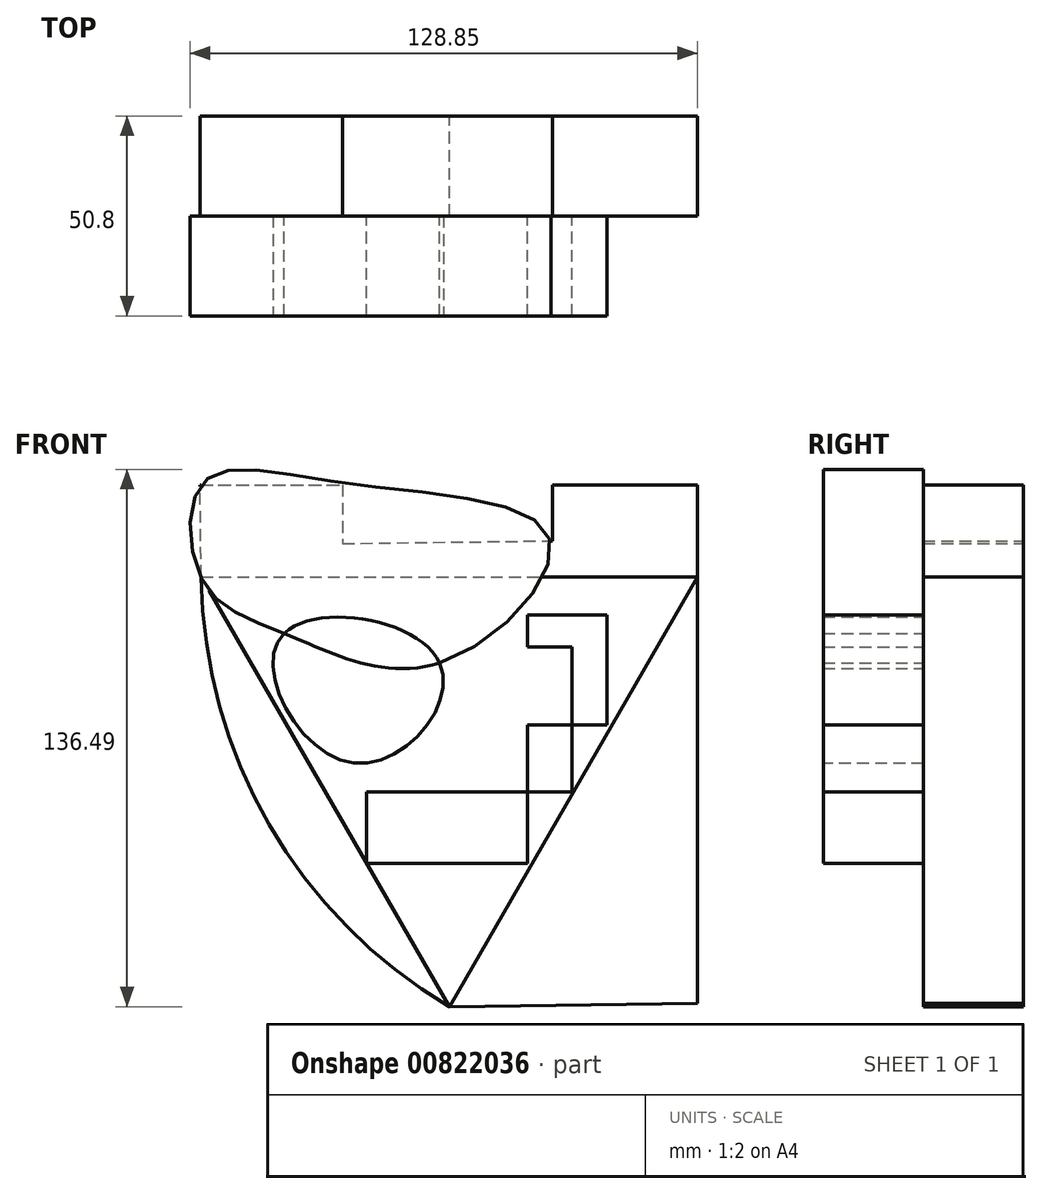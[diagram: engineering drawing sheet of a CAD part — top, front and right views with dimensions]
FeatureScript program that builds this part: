
annotation { "Feature Type Name" : "Feature", "Feature Type Description" : "" }
export const myFeature = defineFeature(function(context is Context, id is Id, definition is map)
    precondition{}
    {
        {
            var Q0;
            Q0=qCreatedBy(makeId("Front.planeOp"),FACE);
            var sketch = newSketch(context, id + "F0", { "sketchPlane" : qUnion([Q0])});
            skCircle(sketch, "E0.cCircle", {"center": v(-2.98, 2.26) * mm, "radius": 36.39 * mm, "construction": true});
            skLineSegment(sketch, "E0.0", {"start": v(-66, 38.65) * mm, "end": v(60.05, 38.65) * mm});
            skLineSegment(sketch, "E0.1", {"start": v(60.05, 38.65) * mm, "end": v(-2.98, -70.52) * mm});
            skLineSegment(sketch, "E0.2", {"start": v(-2.98, -70.52) * mm, "end": v(-66, 38.65) * mm});
            skPoint(sketch, "E0.0.midPoint", {"position": v(-2.98, 38.65) * mm});
            skLineSegment(sketch, "E1", {"start": v(60.05, 38.65) * mm, "end": v(60.05, -69.7) * mm});
            skLineSegment(sketch, "E2", {"start": v(60.05, -69.7) * mm, "end": v(-2.98, -70.52) * mm});
            skLineSegment(sketch, "E3", {"start": v(-66, 38.65) * mm, "end": v(-66.3, 62.08) * mm});
            skLineSegment(sketch, "E4", {"start": v(-66.3, 62.08) * mm, "end": v(-30.07, 62.08) * mm});
            skLineSegment(sketch, "E5", {"start": v(-30.07, 62.08) * mm, "end": v(-30.07, 47.14) * mm});
            skLineSegment(sketch, "E6", {"start": v(-30.07, 47.14) * mm, "end": v(-2.98, 47.49) * mm});
            skLineSegment(sketch, "E7", {"start": v(-2.98, 47.49) * mm, "end": v(-2.98, 62.08) * mm});
            skLineSegment(sketch, "E8", {"start": v(-2.98, 62.08) * mm, "end": v(-2.98, 47.49) * mm});
            skLineSegment(sketch, "E9", {"start": v(-2.98, 47.49) * mm, "end": v(23.3, 47.83) * mm});
            skLineSegment(sketch, "E10", {"start": v(23.3, 47.83) * mm, "end": v(23.3, 62.08) * mm});
            skLineSegment(sketch, "E11", {"start": v(23.3, 62.08) * mm, "end": v(60.05, 62.08) * mm});
            skLineSegment(sketch, "E12", {"start": v(60.05, 62.08) * mm, "end": v(60.05, 38.65) * mm});
            skArc(sketch, "E13", {"start": v(-2.98, 62.08) * mm, "mid": v(-16.52, 68.36) * mm, "end": v(-30.07, 62.08) * mm});
            skArc(sketch, "E14", {"start": v(23.3, 62.08) * mm, "mid": v(10.16, 68.26) * mm, "end": v(-2.98, 62.08) * mm});
            skArc(sketch, "E15", {"start": v(-66, 38.65) * mm, "mid": v(-48.74, -24.16) * mm, "end": v(-2.98, -70.52) * mm});
            skSolve(sketch);
        }
        {
            var Q0;
            Q0=makeQuery(id+"F0.imprint","IMPRINT",FACE,{"disambiguationData":[TD([[makeQuery(id+"F0.imprint","IMPRINT",EDGE,{"derivedFrom":sQuery(id+"F0.wireOp",EDGE,"E0.0")}),1.0]])]});
            var Q1;
            Q1=makeQuery(id+"F0.imprint","IMPRINT",FACE,{"disambiguationData":[TD([[makeQuery(id+"F0.imprint","IMPRINT",EDGE,{"derivedFrom":sQuery(id+"F0.wireOp",EDGE,"E0.2")}),1.0]])]});
            var Q2;
            Q2=makeQuery(id+"F0.imprint","IMPRINT",FACE,{"disambiguationData":[TD([[makeQuery(id+"F0.imprint","IMPRINT",EDGE,{"derivedFrom":sQuery(id+"F0.wireOp",EDGE,"E0.1")}),1.0]])]});
            extrude(context, id + "F1", {"entities" : qUnion([Q0, Q1, Q2]), "depth" : 25.4 * mm, "offsetDistance" : 25.4 * mm});
        }
        {
            var Q0;
            Q0=makeQuery(id+"F1.opExtrude","CAP_FACE",FACE,{"disambiguationData":[OSD([sQuery(id+"F0.wireOp",EDGE,"E0.1"),sQuery(id+"F0.wireOp",EDGE,"E1"),sQuery(id+"F0.wireOp",EDGE,"E2")])],"isStart":false});
            var sketch = newSketch(context, id + "F2", { "sketchPlane" : qUnion([Q0])});
            skSolve(sketch);
        }
        {
            var Q0;
            Q0=makeQuery(id+"F2.imprint","IMPRINT",FACE,{"disambiguationData":[TD([[makeQuery(id+"F2.imprint","IMPRINT",EDGE,{"derivedFrom":makeQuery(id+"F1.opExtrude","CAP_EDGE",EDGE,{"disambiguationData":[OSD([sQuery(id+"F0.wireOp",EDGE,"E0.1")])],"isStart":false})}),1.0]])]});
            var sketch = newSketch(context, id + "F3", { "sketchPlane" : qUnion([Q0])});
            skFitSpline(sketch, "E16", {"points": [v(-45.83, 23.3) * mm, v(-5.4, 16.82) * mm, v(-27.24, -8.65) * mm, v(-45.83, 23.3) * mm]});
            skFitSpline(sketch, "E17", {"points": [v(-65.65, 62.52) * mm, v(-29.66, 62.52) * mm, v(22.5, 48.36) * mm, v(-5.4, 16.82) * mm, v(-44.9, 24.35) * mm, v(-65.24, 37.04) * mm, v(-65.65, 62.52) * mm]});
            skSolve(sketch);
        }
        {
            var Q0;
            {var subQ0=sQuery(id+"F3.wireOp",EDGE,"E17");var subQ1=sQuery(id+"F3.wireOp",EDGE,"E16");var subQ2=makeQuery(id+"F3.imprint","INTERSECT",VERTEX,{"disambiguationData":[OD(0.0)],"derivedFrom":[subQ1,subQ0]});Q0=makeQuery(id+"F3.imprint","IMPRINT",FACE,{"disambiguationData":[TD([[makeQuery(id+"F3.imprint","IMPRINT",EDGE,{"disambiguationData":[TD([[subQ2,1.0]])],"derivedFrom":subQ1}),-1.0]])]});}
            var Q1;
            {var subQ0=sQuery(id+"F3.wireOp",EDGE,"E17");var subQ1=sQuery(id+"F3.wireOp",EDGE,"E16");var subQ2=makeQuery(id+"F3.imprint","INTERSECT",VERTEX,{"disambiguationData":[OD(0.0)],"derivedFrom":[subQ1,subQ0]});Q1=makeQuery(id+"F3.imprint","IMPRINT",FACE,{"disambiguationData":[TD([[makeQuery(id+"F3.imprint","IMPRINT",EDGE,{"disambiguationData":[TD([[subQ2,-1.0]])],"derivedFrom":subQ1}),1.0]])]});}
            extrude(context, id + "F4", {"entities" : qUnion([Q0, Q1]), "depth" : 25.4 * mm, "offsetDistance" : 25.4 * mm});
        }
        {
            var Q0;
            Q0=makeQuery(id+"F1.opExtrude","CAP_FACE",FACE,{"disambiguationData":[OSD([sQuery(id+"F0.wireOp",EDGE,"E0.2"),sQuery(id+"F0.wireOp",EDGE,"E15")])],"isStart":false});
            var sketch = newSketch(context, id + "F5", { "sketchPlane" : qUnion([Q0])});
            skLineSegment(sketch, "E18.bottom", {"start": v(-23.96, -34.16) * mm, "end": v(16.83, -34.16) * mm});
            skLineSegment(sketch, "E18.top", {"start": v(-23.96, -15.93) * mm, "end": v(16.83, -15.93) * mm});
            skLineSegment(sketch, "E18.left", {"start": v(-23.96, -34.16) * mm, "end": v(-23.96, -15.93) * mm});
            skLineSegment(sketch, "E18.right", {"start": v(16.83, -34.16) * mm, "end": v(16.83, -15.93) * mm});
            skLineSegment(sketch, "E19.bottom", {"start": v(16.83, -15.93) * mm, "end": v(28.16, -15.93) * mm});
            skLineSegment(sketch, "E19.top", {"start": v(16.83, 1.05) * mm, "end": v(28.16, 1.05) * mm});
            skLineSegment(sketch, "E19.left", {"start": v(16.83, -15.93) * mm, "end": v(16.83, 1.05) * mm});
            skLineSegment(sketch, "E19.right", {"start": v(28.16, -15.93) * mm, "end": v(28.16, 1.05) * mm});
            skLineSegment(sketch, "E20.bottom", {"start": v(28.16, 1.05) * mm, "end": v(37.05, 1.05) * mm});
            skLineSegment(sketch, "E20.top", {"start": v(28.16, 28.95) * mm, "end": v(37.05, 28.95) * mm});
            skLineSegment(sketch, "E20.left", {"start": v(28.16, 1.05) * mm, "end": v(28.16, 28.95) * mm});
            skLineSegment(sketch, "E20.right", {"start": v(37.05, 1.05) * mm, "end": v(37.05, 28.95) * mm});
            skLineSegment(sketch, "E21.bottom", {"start": v(28.16, 28.95) * mm, "end": v(16.83, 28.95) * mm});
            skLineSegment(sketch, "E21.top", {"start": v(28.16, 20.87) * mm, "end": v(16.83, 20.87) * mm});
            skLineSegment(sketch, "E21.left", {"start": v(28.16, 28.95) * mm, "end": v(28.16, 20.87) * mm});
            skLineSegment(sketch, "E21.right", {"start": v(16.83, 28.95) * mm, "end": v(16.83, 20.87) * mm});
            skSolve(sketch);
        }
        {
            var Q0;
            Q0=makeQuery(id+"F5.imprint","IMPRINT",FACE,{"disambiguationData":[TD([[makeQuery(id+"F5.imprint","IMPRINT",EDGE,{"derivedFrom":sQuery(id+"F5.wireOp",EDGE,"E21.bottom")}),1.0]])]});
            var Q1;
            Q1=makeQuery(id+"F5.imprint","IMPRINT",FACE,{"disambiguationData":[TD([[makeQuery(id+"F5.imprint","IMPRINT",EDGE,{"derivedFrom":sQuery(id+"F5.wireOp",EDGE,"E20.bottom")}),1.0]])]});
            var Q2;
            Q2=makeQuery(id+"F5.imprint","IMPRINT",FACE,{"disambiguationData":[TD([[makeQuery(id+"F5.imprint","IMPRINT",EDGE,{"derivedFrom":sQuery(id+"F5.wireOp",EDGE,"E19.bottom")}),1.0]])]});
            var Q3;
            Q3=makeQuery(id+"F5.imprint","IMPRINT",FACE,{"disambiguationData":[TD([[makeQuery(id+"F5.imprint","IMPRINT",EDGE,{"derivedFrom":sQuery(id+"F5.wireOp",EDGE,"E18.bottom")}),1.0]])]});
            extrude(context, id + "F6", {"entities" : qUnion([Q0, Q1, Q2, Q3]), "depth" : 25.4 * mm, "offsetDistance" : 25.4 * mm});
        }
    });
